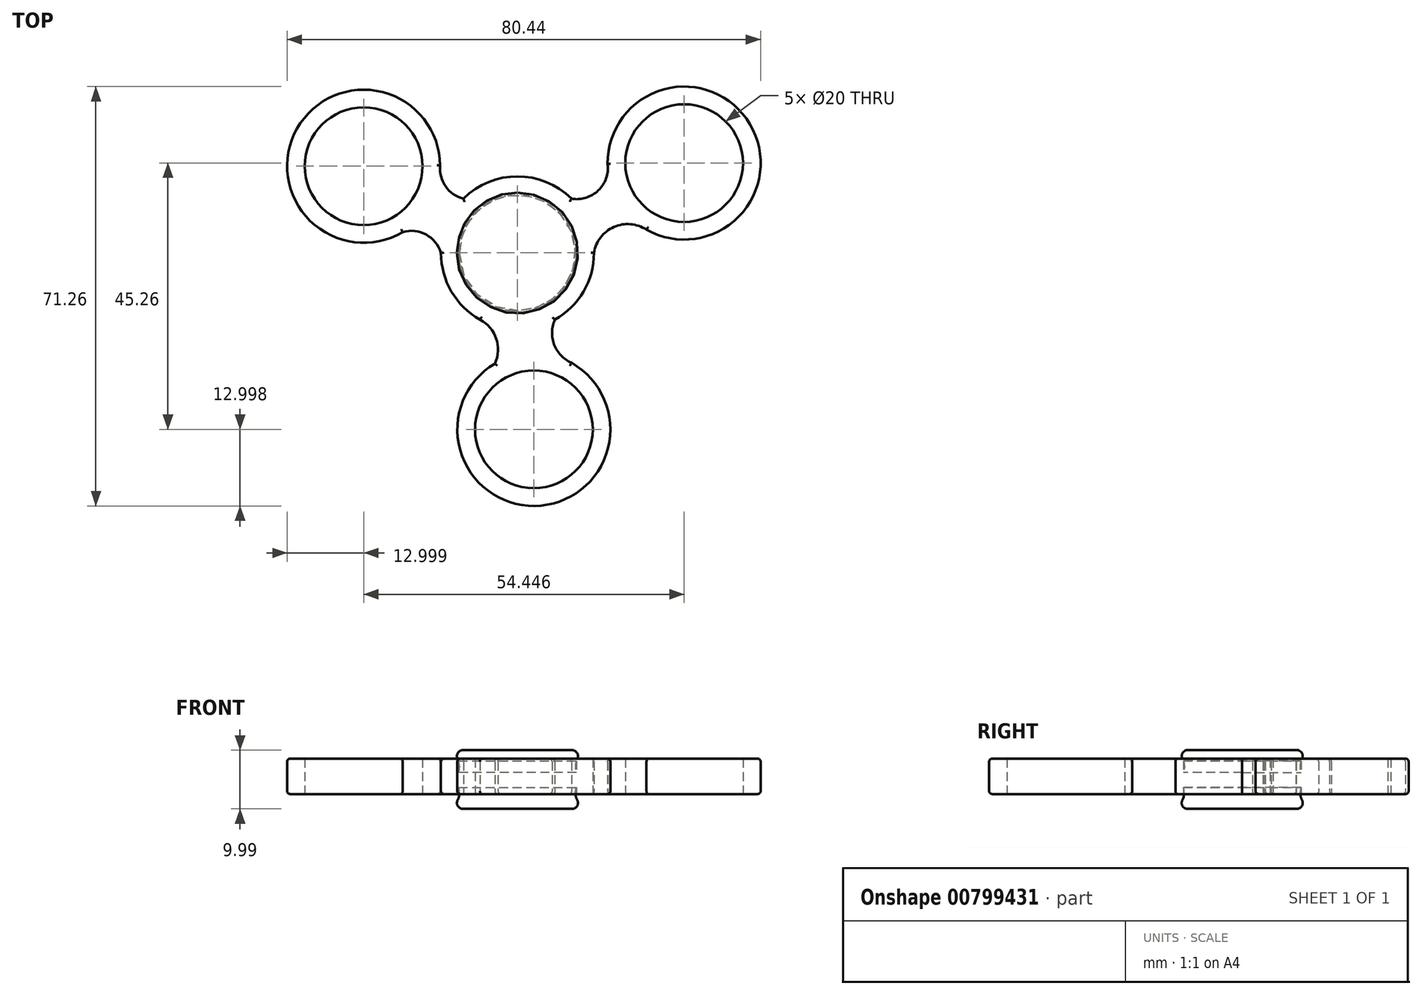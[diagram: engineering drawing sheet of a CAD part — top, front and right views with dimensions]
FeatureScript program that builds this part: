
annotation { "Feature Type Name" : "Feature", "Feature Type Description" : "" }
export const myFeature = defineFeature(function(context is Context, id is Id, definition is map)
    precondition{}
    {
        {
            var Q0;
            Q0=qCreatedBy(makeId("Top.planeOp"),FACE);
            var sketch = newSketch(context, id + "F0", { "sketchPlane" : qUnion([Q0])});
            skPoint(sketch, "E0.0.midPoint", {"position": v(15.55, -7.36) * mm});
            skCircle(sketch, "E1", {"center": v(0, 0) * mm, "radius": 10 * mm});
            skCircle(sketch, "E2", {"center": v(28.31, 15.27) * mm, "radius": 10 * mm});
            skCircle(sketch, "E3", {"center": v(2.8, -30) * mm, "radius": 10 * mm});
            skCircle(sketch, "E4", {"center": v(-26.13, 14.74) * mm, "radius": 10 * mm});
            skArc(sketch, "E5.0", {"start": v(-13.15, 14.02) * mm, "mid": v(-37.24, 21.49) * mm, "end": v(-19.52, 3.54) * mm});
            skArc(sketch, "E6.0", {"start": v(21.93, 3.95) * mm, "mid": v(39.27, 22.27) * mm, "end": v(15.36, 14.22) * mm});
            skArc(sketch, "E7.0", {"start": v(-3.82, -18.8) * mm, "mid": v(2.92, -43) * mm, "end": v(9.18, -18.67) * mm});
            skArc(sketch, "E8.0", {"start": v(-13, 0) * mm, "mid": v(-11.22, -6.57) * mm, "end": v(-6.36, -11.34) * mm});
            skArc(sketch, "E9", {"start": v(-3.82, -18.8) * mm, "mid": v(-3.6, -14.56) * mm, "end": v(-6.36, -11.34) * mm});
            skArc(sketch, "E10", {"start": v(6.36, -11.34) * mm, "mid": v(6.25, -15.59) * mm, "end": v(9.18, -18.67) * mm});
            skArc(sketch, "E11", {"start": v(-13, 0) * mm, "mid": v(-15.53, 3.11) * mm, "end": v(-19.52, 3.54) * mm});
            skArc(sketch, "E12", {"start": v(-13.13, 14.87) * mm, "mid": v(-12.2, 11.3) * mm, "end": v(-9.17, 9.21) * mm});
            skArc(sketch, "E13", {"start": v(9.17, 9.21) * mm, "mid": v(13.74, 10.62) * mm, "end": v(15.32, 15.14) * mm});
            skArc(sketch, "E14", {"start": v(21.93, 3.95) * mm, "mid": v(16.39, 4.4) * mm, "end": v(13, 0) * mm});
            skArc(sketch, "E15.trimOffspring", {"start": v(6.36, -11.34) * mm, "mid": v(11.22, -6.57) * mm, "end": v(13, 0) * mm});
            skArc(sketch, "E16.trimOffspring", {"start": v(9.17, 9.21) * mm, "mid": v(0, 13) * mm, "end": v(-9.17, 9.21) * mm});
            skSolve(sketch);
        }
        {
            var Q0;
            Q0=makeQuery(id+"F0.imprint","IMPRINT",FACE,{"disambiguationData":[TD([[makeQuery(id+"F0.imprint","IMPRINT",EDGE,{"derivedFrom":sQuery(id+"F0.wireOp",EDGE,"E1")}),-1.0]])]});
            extrude(context, id + "F1", {"entities" : qUnion([Q0]), "depth" : 6 * mm, "offsetDistance" : 25 * mm});
        }
        {
            var Q0;
            Q0=makeQuery(id+"F1.opExtrude","CAP_EDGE",EDGE,{"disambiguationData":[OSD([sQuery(id+"F0.wireOp",EDGE,"E7.0")])],"isStart":false});
            var Q1;
            Q1=makeQuery(id+"F1.opExtrude","CAP_EDGE",EDGE,{"disambiguationData":[OSD([sQuery(id+"F0.wireOp",EDGE,"E10")])],"isStart":false});
            var Q2;
            Q2=makeQuery(id+"F1.opExtrude","CAP_EDGE",EDGE,{"disambiguationData":[OSD([sQuery(id+"F0.wireOp",EDGE,"E15.trimOffspring")])],"isStart":false});
            var Q3;
            Q3=makeQuery(id+"F1.opExtrude","CAP_EDGE",EDGE,{"disambiguationData":[OSD([sQuery(id+"F0.wireOp",EDGE,"E14")])],"isStart":false});
            var Q4;
            Q4=makeQuery(id+"F1.opExtrude","CAP_EDGE",EDGE,{"disambiguationData":[OSD([sQuery(id+"F0.wireOp",EDGE,"E6.0")])],"isStart":false});
            var Q5;
            Q5=makeQuery(id+"F1.opExtrude","CAP_EDGE",EDGE,{"disambiguationData":[OSD([sQuery(id+"F0.wireOp",EDGE,"E13")])],"isStart":false});
            var Q6;
            Q6=makeQuery(id+"F1.opExtrude","CAP_EDGE",EDGE,{"disambiguationData":[OSD([sQuery(id+"F0.wireOp",EDGE,"E16.trimOffspring")])],"isStart":false});
            var Q7;
            Q7=makeQuery(id+"F1.opExtrude","CAP_EDGE",EDGE,{"disambiguationData":[OSD([sQuery(id+"F0.wireOp",EDGE,"E12")])],"isStart":false});
            var Q8;
            Q8=makeQuery(id+"F1.opExtrude","CAP_EDGE",EDGE,{"disambiguationData":[OSD([sQuery(id+"F0.wireOp",EDGE,"E5.0")])],"isStart":false});
            var Q9;
            Q9=makeQuery(id+"F1.opExtrude","CAP_EDGE",EDGE,{"disambiguationData":[OSD([sQuery(id+"F0.wireOp",EDGE,"E11")])],"isStart":false});
            var Q10;
            Q10=makeQuery(id+"F1.opExtrude","CAP_EDGE",EDGE,{"disambiguationData":[OSD([sQuery(id+"F0.wireOp",EDGE,"E8.0")])],"isStart":false});
            var Q11;
            Q11=makeQuery(id+"F1.opExtrude","CAP_EDGE",EDGE,{"disambiguationData":[OSD([sQuery(id+"F0.wireOp",EDGE,"E9")])],"isStart":false});
            var Q12;
            Q12=makeQuery(id+"F1.opExtrude","CAP_EDGE",EDGE,{"disambiguationData":[OSD([sQuery(id+"F0.wireOp",EDGE,"E5.0")])],"isStart":true});
            var Q13;
            Q13=makeQuery(id+"F1.opExtrude","CAP_EDGE",EDGE,{"disambiguationData":[OSD([sQuery(id+"F0.wireOp",EDGE,"E11")])],"isStart":true});
            var Q14;
            Q14=makeQuery(id+"F1.opExtrude","CAP_EDGE",EDGE,{"disambiguationData":[OSD([sQuery(id+"F0.wireOp",EDGE,"E8.0")])],"isStart":true});
            var Q15;
            Q15=makeQuery(id+"F1.opExtrude","CAP_EDGE",EDGE,{"disambiguationData":[OSD([sQuery(id+"F0.wireOp",EDGE,"E9")])],"isStart":true});
            var Q16;
            Q16=makeQuery(id+"F1.opExtrude","CAP_EDGE",EDGE,{"disambiguationData":[OSD([sQuery(id+"F0.wireOp",EDGE,"E12")])],"isStart":true});
            var Q17;
            Q17=makeQuery(id+"F1.opExtrude","CAP_EDGE",EDGE,{"disambiguationData":[OSD([sQuery(id+"F0.wireOp",EDGE,"E16.trimOffspring")])],"isStart":true});
            var Q18;
            Q18=makeQuery(id+"F1.opExtrude","CAP_EDGE",EDGE,{"disambiguationData":[OSD([sQuery(id+"F0.wireOp",EDGE,"E13")])],"isStart":true});
            var Q19;
            Q19=makeQuery(id+"F1.opExtrude","CAP_EDGE",EDGE,{"disambiguationData":[OSD([sQuery(id+"F0.wireOp",EDGE,"E6.0")])],"isStart":true});
            var Q20;
            Q20=makeQuery(id+"F1.opExtrude","CAP_EDGE",EDGE,{"disambiguationData":[OSD([sQuery(id+"F0.wireOp",EDGE,"E14")])],"isStart":true});
            var Q21;
            Q21=makeQuery(id+"F1.opExtrude","CAP_EDGE",EDGE,{"disambiguationData":[OSD([sQuery(id+"F0.wireOp",EDGE,"E15.trimOffspring")])],"isStart":true});
            var Q22;
            Q22=makeQuery(id+"F1.opExtrude","CAP_EDGE",EDGE,{"disambiguationData":[OSD([sQuery(id+"F0.wireOp",EDGE,"E10")])],"isStart":true});
            var Q23;
            Q23=makeQuery(id+"F1.opExtrude","CAP_EDGE",EDGE,{"disambiguationData":[OSD([sQuery(id+"F0.wireOp",EDGE,"E7.0")])],"isStart":true});
            fillet(context, id + "F2", {"entities" : qUnion([Q0, Q1, Q2, Q3, Q4, Q5, Q6, Q7, Q8, Q9, Q10, Q11, Q12, Q13, Q14, Q15, Q16, Q17, Q18, Q19, Q20, Q21, Q22, Q23]), "radius" : 0.5 * mm, "allowEdgeOverflow" : false});
        }
        {
            var Q0;
            Q0=qCreatedBy(makeId("Right.planeOp"),FACE);
            var sketch = newSketch(context, id + "F3", { "sketchPlane" : qUnion([Q0])});
            skLineSegment(sketch, "E17", {"start": v(-12.61, -2.53) * mm, "end": v(0, -2.53) * mm});
            skLineSegment(sketch, "E18", {"start": v(0, -2.53) * mm, "end": v(0, 7.46) * mm});
            skLineSegment(sketch, "E19", {"start": v(0, 7.46) * mm, "end": v(-12.64, 7.46) * mm});
            skArc(sketch, "E20", {"start": v(-10, 3.64) * mm, "mid": v(-10.32, 6.24) * mm, "end": v(-12.64, 7.46) * mm});
            skArc(sketch, "E21", {"start": v(-12.61, -2.53) * mm, "mid": v(-10.36, -1.36) * mm, "end": v(-10, 1.14) * mm});
            skLineSegment(sketch, "E22", {"start": v(-10, 1.14) * mm, "end": v(-10, 3.64) * mm});
            skSolve(sketch);
        }
        {
            var Q0;
            Q0=makeQuery(id+"F3.imprint","IMPRINT",FACE,{"disambiguationData":[TD([[makeQuery(id+"F3.imprint","IMPRINT",EDGE,{"derivedFrom":sQuery(id+"F3.wireOp",EDGE,"E17")}),1.0]])]});
            var Q1;
            Q1=sQuery(id+"F3.wireOp",EDGE,"E18");
            revolve(context, id + "F4", {"operationType" : NewBodyOperationType.ADD, "surfaceOperationType" : NewSurfaceOperationType.NEW, "entities" : qUnion([Q0]), "axis" : qUnion([Q1]), "revolveType" : RevolveType.FULL});
        }
        {
            var Q0;
            Q0=makeQuery(id+"F4.opRevolve","SWEPT_EDGE",EDGE,{"disambiguationData":[OSD([sQuery(id+"F3.wireOp",EDGE,"E19"),sQuery(id+"F3.wireOp",EDGE,"E20")])]});
            var Q1;
            Q1=makeQuery(id+"F4.opRevolve","SWEPT_EDGE",EDGE,{"disambiguationData":[OSD([sQuery(id+"F3.wireOp",EDGE,"E17"),sQuery(id+"F3.wireOp",EDGE,"E21")])]});
            fillet(context, id + "F5", {"entities" : qUnion([Q0, Q1]), "radius" : 1 * mm, "tangentPropagation" : true, "allowEdgeOverflow" : false});
        }
    });
